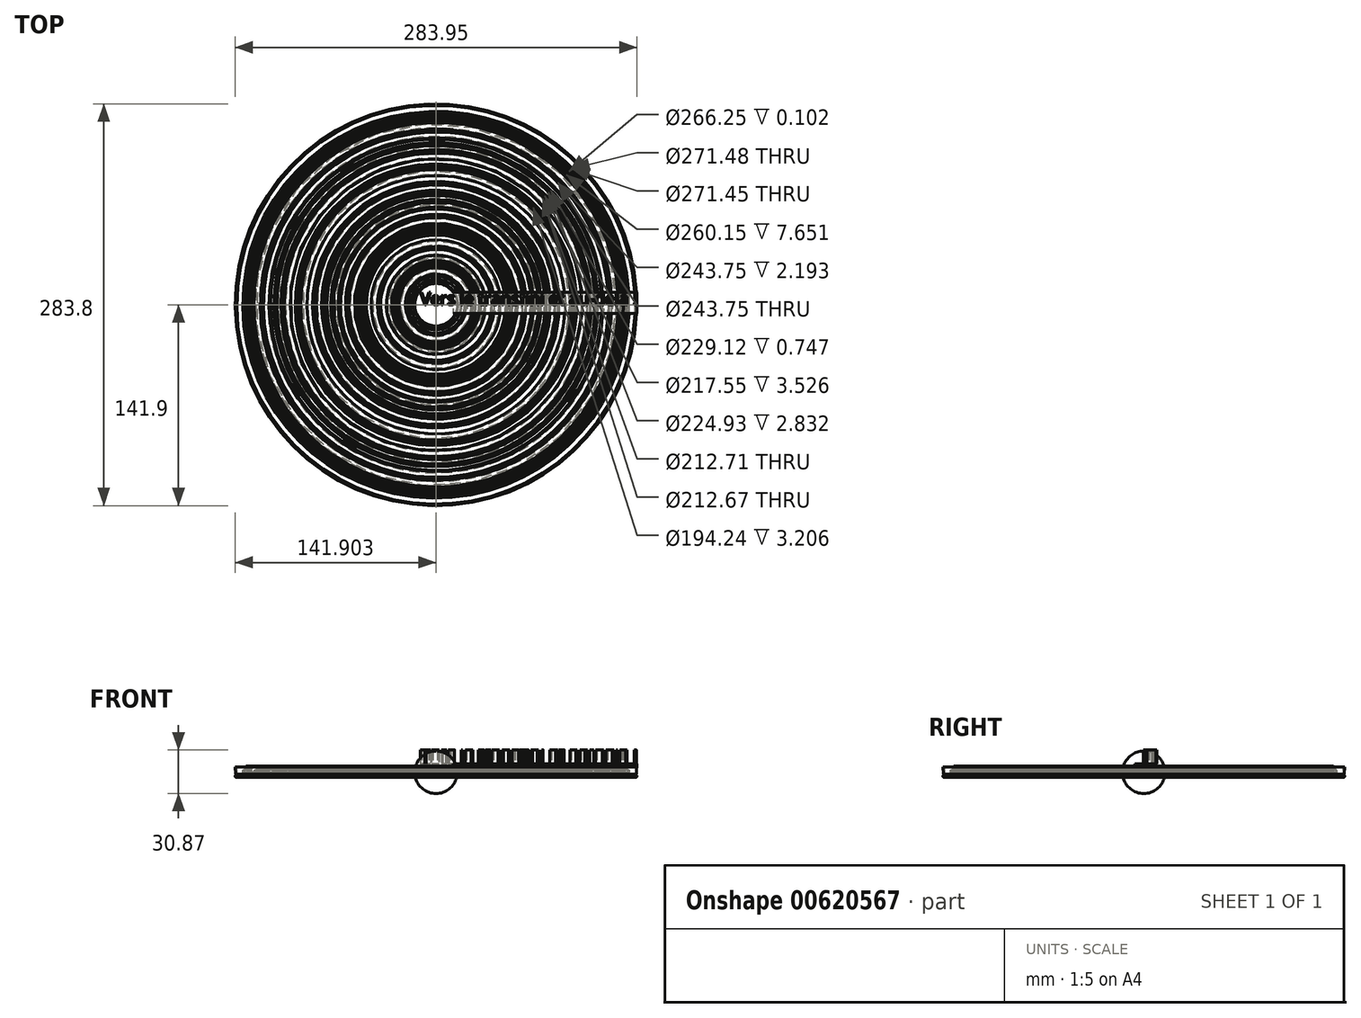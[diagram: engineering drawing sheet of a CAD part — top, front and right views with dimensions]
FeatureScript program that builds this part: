
annotation { "Feature Type Name" : "Feature", "Feature Type Description" : "" }
export const myFeature = defineFeature(function(context is Context, id is Id, definition is map)
    precondition{}
    {
        {
            var Q0;
            Q0=qCreatedBy(makeId("Front.planeOp"),FACE);
            var sketch = newSketch(context, id + "F0", { "sketchPlane" : qUnion([Q0])});
            skLineSegment(sketch, "E0", {"start": v(-24.08, 34.12) * mm, "end": v(-24.08, 4.12) * mm});
            skPoint(sketch, "E1", {"position": v(-24.08, 19.12) * mm});
            skArc(sketch, "E2", {"start": v(-24.08, 4.12) * mm, "mid": v(-9.08, 19.12) * mm, "end": v(-24.08, 34.12) * mm});
            skText(sketch, "E3", { "text": "Vers le transfini et au-delà !", "fontName": "OpenSans-Regular.ttf"});
            const initialGuessF0  = {"E3": [-0.00907, 0.0158, 1, 0, 0.00725]};
            skSetInitialGuess(sketch, initialGuessF0);
            skSolve(sketch);
        }
        {
            var Q0;
            Q0 = qSketchRegion(id + "F0", true);
            var Q1;
            Q1=sQuery(id+"F0.wireOp",EDGE,"E0");
            revolve(context, id + "F1", {"entities" : qUnion([Q0]), "axis" : qUnion([Q1]), "revolveType" : RevolveType.FULL});
        }
        {
            var Q0;
            Q0=makeQuery(id+"F1.opRevolve","SWEPT_FACE",FACE,{"disambiguationData":[OSD([sQuery(id+"F0.wireOp",EDGE,"E3.sketch_text.stroke-0")])]});
            var sketch = newSketch(context, id + "F2", { "sketchPlane" : qUnion([Q0])});
            skLineSegment(sketch, "E4.bottom", {"start": v(-12.03, 8.72) * mm, "end": v(117.97, 8.72) * mm});
            skLineSegment(sketch, "E4.top", {"start": v(-12.03, -6.28) * mm, "end": v(117.97, -6.28) * mm});
            skLineSegment(sketch, "E4.left", {"start": v(-12.03, 8.72) * mm, "end": v(-12.03, -6.28) * mm});
            skLineSegment(sketch, "E4.right", {"start": v(117.97, 8.72) * mm, "end": v(117.97, -6.28) * mm});
            skSolve(sketch);
        }
        {
            var Q0;
            Q0 = qSketchRegion(id + "F2", true);
            extrude(context, id + "F3", {"entities" : qUnion([Q0]), "depth" : 2 * mm, "offsetDistance" : 25 * mm});
        }
        {
            var Q0;
            Q0=makeQuery(id+"F3.opExtrude","CAP_FACE",FACE,{"disambiguationData":[OSD([sQuery(id+"F2.wireOp",EDGE,"E4.bottom"),sQuery(id+"F2.wireOp",EDGE,"E4.top"),sQuery(id+"F2.wireOp",EDGE,"E4.left"),sQuery(id+"F2.wireOp",EDGE,"E4.right")])],"isStart":false});
            var sketch = newSketch(context, id + "F4", { "sketchPlane" : qUnion([Q0])});
            skText(sketch, "E5", { "text": "Vers le transfini et au-delà !", "fontName": "OpenSans-Regular.ttf"});
            const initialGuessF4  = {"E5": [-0.03518, 0, 1, 0, 0.00872]};
            skSetInitialGuess(sketch, initialGuessF4);
            skSolve(sketch);
        }
        {
            var Q0;
            Q0 = qSketchRegion(id + "F4", true);
            extrude(context, id + "F5", {"entities" : qUnion([Q0]), "depth" : 10 * mm, "offsetDistance" : 25 * mm});
        }
    });
